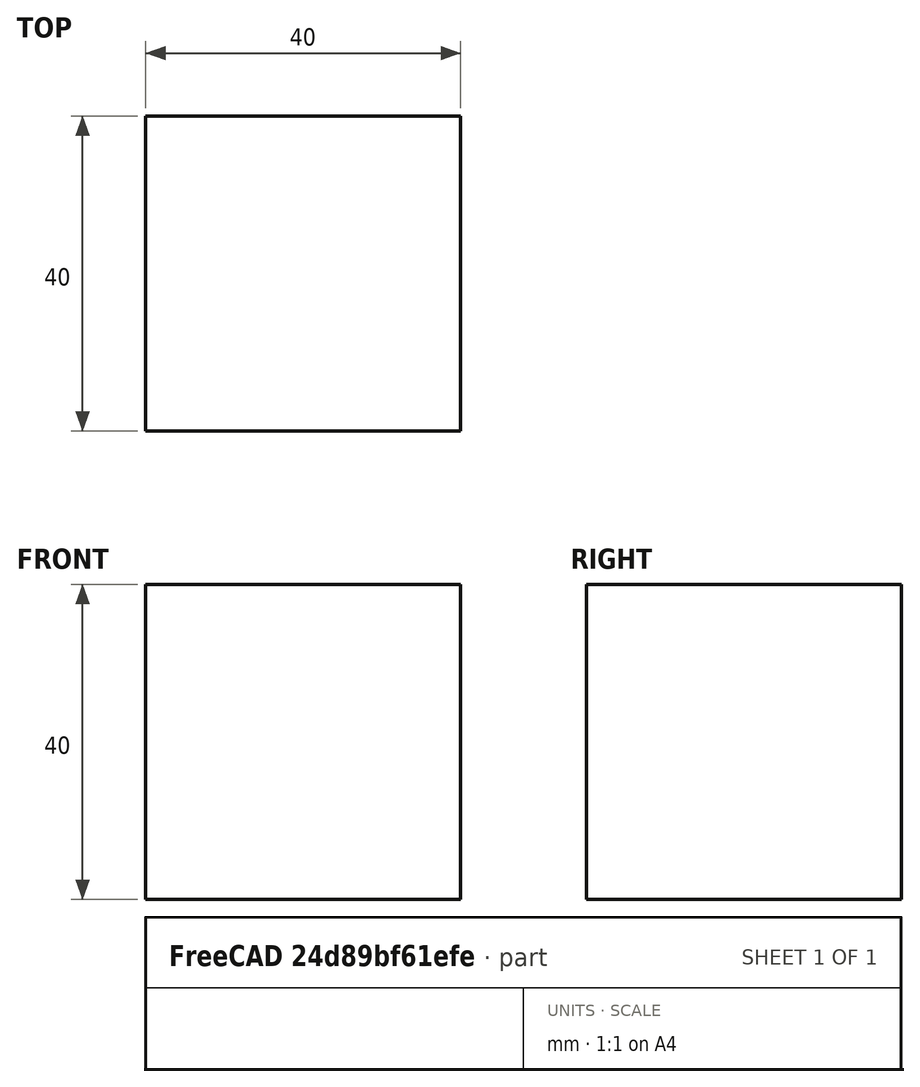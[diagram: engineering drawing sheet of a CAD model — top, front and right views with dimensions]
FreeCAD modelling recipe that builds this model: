
FCSTD DOCUMENT  (FreeCAD 1.0R39109 (Git))
Label: cube_40mm
License: All rights reserved
LicenseURL: https://en.wikipedia.org/wiki/All_rights_reserved
objects: Sketcher::SketchObject×1, PartDesign::Pad×1, PartDesign::Body×1
note: 6 computed .brp shape members not serialized (recipe doc carries the construction recipe); baked Part::Feature solids carry a one-line shape summary decoded from their .brp

FEATURE [Sketcher::SketchObject] Sketch
  ArcFitTolerance = 1e-06
  AttachmentSupport = -> [XY_Plane]
  FullyConstrained = true
  MakeInternals = false
  MapMode = 5
  sketch-geometry (4):
    g0: LineSegment StartX=0 StartY=0 StartZ=0 EndX=40 EndY=0 EndZ=0
    g1: LineSegment StartX=40 StartY=0 StartZ=0 EndX=40 EndY=40 EndZ=0
    g2: LineSegment StartX=40 StartY=40 StartZ=0 EndX=0 EndY=40 EndZ=0
    g3: LineSegment StartX=0 StartY=40 StartZ=0 EndX=0 EndY=0 EndZ=0
  constraints (11):
    c: Coincident(g0,g1)
    c: Coincident(g1,g2)
    c: Coincident(g2,g3)
    c: Coincident(g3,g0)
    c: Horizontal(g0)
    c: Horizontal(g2)
    c: Vertical(g1)
    c: Vertical(g3)
    c: Distance(g1,g3) = 40
    c: Distance(g0,g2) = 40
    c: Coincident(g0,g-1)
FEATURE [PartDesign::Pad] Pad
  Direction = (0,0,1)
  Length = 40
  Length2 = 10
  Profile = -> Sketch
  ReferenceAxis = -> Sketch [N_Axis]
  Refine = true
  Suppressed = false
  Type = 0
FEATURE [PartDesign::Body] Body
  AllowCompound = false
  Group = -> [Sketch,Pad]
  Origin = -> Origin
  Tip = -> Pad
